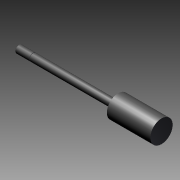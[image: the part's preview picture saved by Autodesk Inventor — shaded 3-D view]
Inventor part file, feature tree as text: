
AUTODESK INVENTOR PART (.ipt)
format: ipt  version: 2012 (Build 160160000, 160)  size: 129,536 bytes
history: native  units: in
note: dims shown in document units (in); Inventor stores cm internally (conversion verified against a paired STEP export)
features: other x70, revolve x3, sketch x3
ambient origin geometry x8: Origin, YZ Plane, XZ Plane, XY Plane, X Axis, Y Axis, Z Axis, Center Point
bodies: Solid1 (feature_tree)
feature tree (76):
  revolve  "Revolution1"  Angle=360.0deg
  revolve  "Revolution2"  [1 undecoded]
  revolve  "Revolution3"  [1 undecoded]
  other  "rod_cp_XY"
  other  "rod_cp_YZ"
  other  "rod_cp_ZX"
  other  "rod_cp_X"
  other  "rod_cp_Y"
  other  "rod_cp_Z"
  other  "rod_cp_Center"
  other  "to_rod_clevis_XY"
  other  "to_rod_clevis_YZ"
  other  "to_rod_clevis_ZX"
  other  "to_rod_clevis_X"
  other  "to_rod_clevis_Y"
  other  "to_rod_clevis_Z"
  other  "to_rod_clevis_Center"
  other  "rl2_XY"
  other  "rl2_YZ"
  other  "rl2_ZX"
  other  "rl2_X"
  other  "rl2_Y"
  other  "rl2_Z"
  other  "rl2_Center"
  other  "rl1_XY"
  other  "rl1_YZ"
  other  "rl1_ZX"
  other  "rl1_X"
  other  "rl1_Y"
  other  "rl1_Z"
  other  "rl1_Center"
  other  "thd1_XY"
  other  "thd1_YZ"
  other  "thd1_ZX"
  other  "thd1_X"
  other  "thd1_Y"
  other  "thd1_Z"
  other  "thd1_Center"
  other  "thd2_XY"
  other  "thd2_YZ"
  other  "thd2_ZX"
  other  "thd2_X"
  other  "thd2_Y"
  other  "thd2_Z"
  other  "thd2_Center"
  other  "dia1_XY"
  other  "dia1_YZ"
  other  "dia1_ZX"
  other  "dia1_X"
  other  "dia1_Y"
  other  "dia1_Z"
  other  "dia1_Center"
  other  "dia2_XY"
  other  "dia2_YZ"
  other  "dia2_ZX"
  other  "dia2_X"
  other  "dia2_Y"
  other  "dia2_Z"
  other  "dia2_Center"
  other  "dia12_XY"
  other  "dia12_YZ"
  other  "dia12_ZX"
  other  "dia12_X"
  other  "dia12_Y"
  other  "dia12_Z"
  other  "dia12_Center"
  other  "dia22_XY"
  other  "dia22_YZ"
  other  "dia22_ZX"
  other  "dia22_X"
  other  "dia22_Y"
  other  "dia22_Z"
  other  "dia22_Center"
  sketch  "Sketch_1"  dims[d0=360.0deg d1=360.0deg]
  sketch  "Sketch_3"  dims[d2=360.0deg]
  sketch  "Sketch_30"
note: 2 required parameter values undecoded (feature->parameter linkage not recoverable at this tier; creation-order binding heuristic only, values carry confidence <= 0.55)
